FCSTD DOCUMENT  (FreeCAD 0.20R29603 (Git))
Label: Case
License: All rights reserved
LicenseURL: http://en.wikipedia.org/wiki/All_rights_reserved
objects: Part::Feature×4, Part::Refine×1, Part::Compound×1, Part::Box×1
note: 7 computed .brp shape members not serialized (recipe doc carries the construction recipe); baked Part::Feature solids carry a one-line shape summary decoded from their .brp

FEATURE [Part::Feature] SpectDrone_1001  label="SpectDrone 002"
  shape: large baked B-rep (67 MB .brp); summary skipped
FEATURE [Part::Feature] SpectDroneControl_1001  label="SpectDroneControl 002"
  Placement = pos=(0,0,11.25) rot=(0,0,1;0rad)
  shape: bbox 101.6 x 73.67 x 14.11 mm, 5388 faces, 102 solids (baked)
FEATURE [Part::Feature] TestComponents_1001  label="TestComponents 002"
  Placement = pos=(0,0,-11.25) rot=(0,0,1;0rad)
  shape: bbox 101.6 x 73.66 x 14.56 mm, 4258 faces, 74 solids (baked)
FEATURE [Part::Refine] SpectDrone_1001001  label="SpectDrone 003"
  Source = -> SpectDrone_1001
FEATURE [Part::Compound] Compound
  Links = -> [SpectDrone_1001001]
FEATURE [Part::Feature] Compound001
  shape: large baked B-rep (68 MB .brp); summary skipped
FEATURE [Part::Box] Box  label="Cube"
  AttacherType = Attacher::AttachEngine3D
  Height = 42
  Length = 258
  Placement = pos=(-200,-38,-21) rot=(0,0,1;0rad)
  Width = 76
